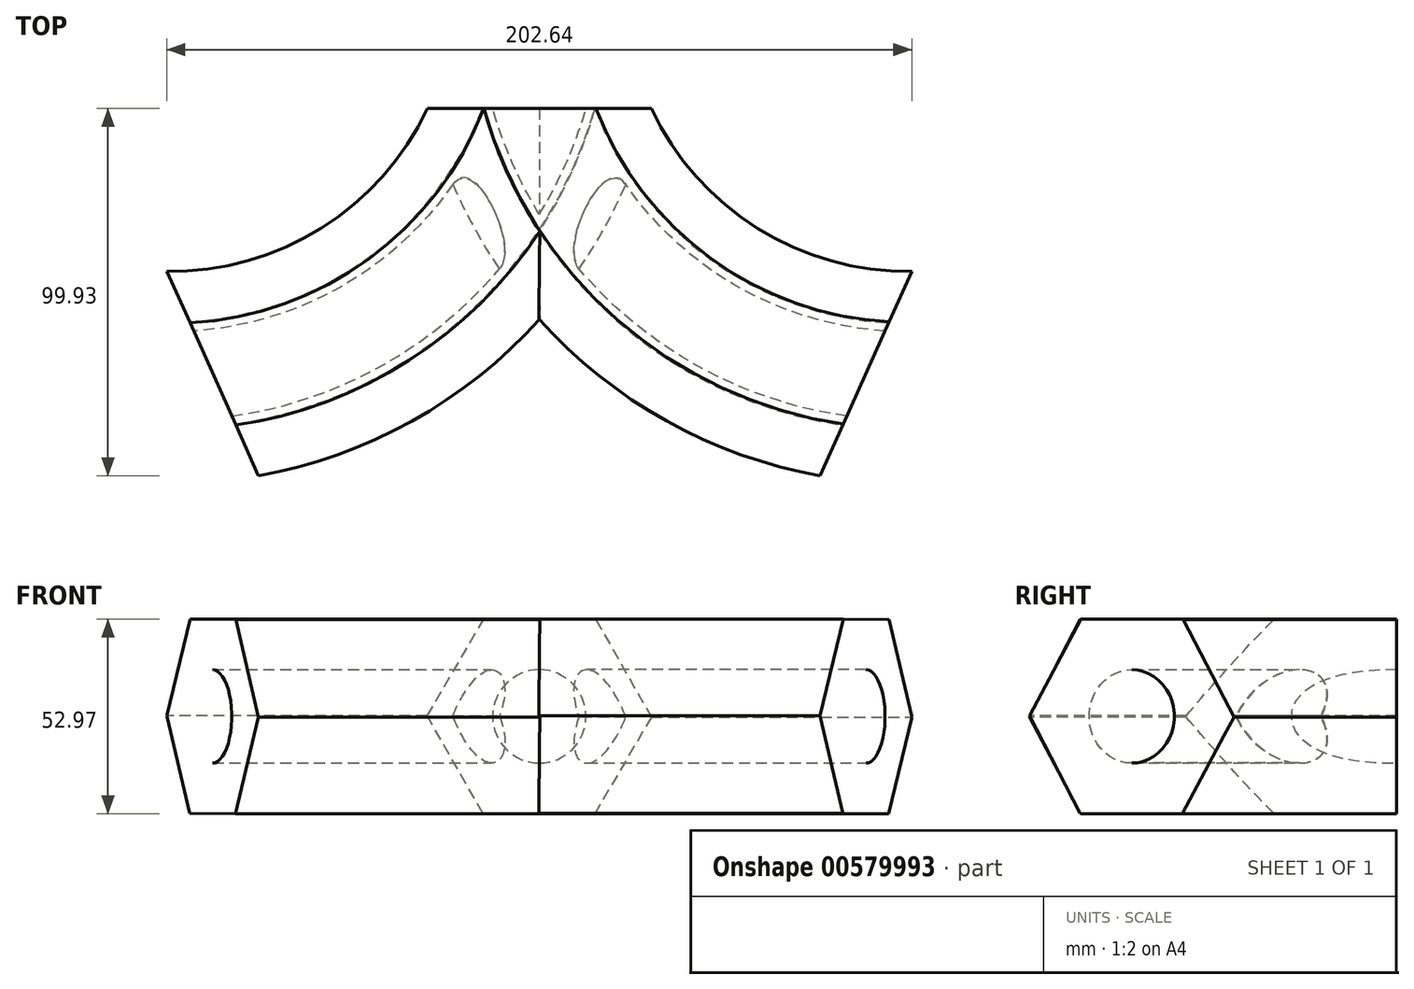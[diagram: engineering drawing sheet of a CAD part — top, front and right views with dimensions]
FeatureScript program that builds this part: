
annotation { "Feature Type Name" : "Feature", "Feature Type Description" : "" }
export const myFeature = defineFeature(function(context is Context, id is Id, definition is map)
    precondition{}
    {
        {
            var Q0;
            Q0=qCreatedBy(makeId("Front.planeOp"),FACE);
            var sketch = newSketch(context, id + "F0", { "sketchPlane" : qUnion([Q0])});
            skCircle(sketch, "E0.cCircle", {"center": v(0, 26.89) * mm, "radius": 26.4 * mm, "construction": true});
            skLineSegment(sketch, "E0.0", {"start": v(-15.4, 0.58) * mm, "end": v(-30.48, 27.07) * mm});
            skLineSegment(sketch, "E0.1", {"start": v(-30.48, 27.07) * mm, "end": v(-15.08, 53.37) * mm});
            skLineSegment(sketch, "E0.2", {"start": v(-15.08, 53.37) * mm, "end": v(15.4, 53.2) * mm});
            skLineSegment(sketch, "E0.3", {"start": v(15.4, 53.2) * mm, "end": v(30.48, 26.7) * mm});
            skLineSegment(sketch, "E0.4", {"start": v(30.48, 26.7) * mm, "end": v(15.08, 0.4) * mm});
            skLineSegment(sketch, "E0.5", {"start": v(15.08, 0.4) * mm, "end": v(-15.4, 0.58) * mm});
            skPoint(sketch, "E0.0.midPoint", {"position": v(-22.94, 13.82) * mm});
            skCircle(sketch, "E1", {"center": v(0, 26.89) * mm, "radius": 12.7 * mm});
            skSolve(sketch);
        }
        {
            var Q0;
            Q0=qCreatedBy(makeId("Top.planeOp"),FACE);
            var sketch = newSketch(context, id + "F1", { "sketchPlane" : qUnion([Q0])});
            skArc(sketch, "E2", {"start": v(-88.86, -72.11) * mm, "mid": v(-33.77, -49.2) * mm, "end": v(0, 0) * mm});
            skArc(sketch, "E3.MirrorCS", {"start": v(88.86, -72.11) * mm, "mid": v(33.77, -49.2) * mm, "end": v(0, 0) * mm});
            skSolve(sketch);
        }
        {
            var Q0;
            Q0=makeQuery(id+"F0.imprint","IMPRINT",FACE,{"disambiguationData":[TD([[makeQuery(id+"F0.imprint","IMPRINT",EDGE,{"derivedFrom":sQuery(id+"F0.wireOp",EDGE,"E0.0")}),-1.0]])]});
            var Q1;
            Q1=sQuery(id+"F1.wireOp",EDGE,"E3.MirrorCS");
            sweep(context, id + "F2", {"profiles" : qUnion([Q0]), "path" : qUnion([Q1])});
        }
        {
            var Q0;
            Q0=makeQuery(id+"F0.imprint","IMPRINT",FACE,{"disambiguationData":[TD([[makeQuery(id+"F0.imprint","IMPRINT",EDGE,{"derivedFrom":sQuery(id+"F0.wireOp",EDGE,"E0.0")}),-1.0]])]});
            var Q1;
            Q1=sQuery(id+"F1.wireOp",EDGE,"E2");
            sweep(context, id + "F3", {"operationType" : NewBodyOperationType.ADD, "profiles" : qUnion([Q0]), "path" : qUnion([Q1])});
        }
    });
